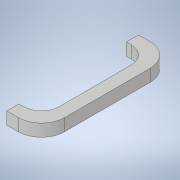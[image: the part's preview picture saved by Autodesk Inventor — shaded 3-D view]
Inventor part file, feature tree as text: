
AUTODESK INVENTOR PART (.ipt)
format: ipt  version: 2020 (Build 240168000, 168)  size: 124,416 bytes
history: native  units: mm
features: extrude x1, fillet x1, hole x1, mirror x1, sketch x1
ambient origin geometry x8: Origin, YZ Plane, XZ Plane, XY Plane, X Axis, Y Axis, Z Axis, Center Point
bodies: Solid1 (feature_tree)
feature tree (5):
  extrude  "Extrusion1"  Depth=30.0mm
  fillet  "Fillet2"  Radius=15.0mm
  hole  "Hole2"  [1 undecoded]
  mirror  "Mirror2"
  sketch  "Sketch1"  dims[d0=114.0mm d1=30.0mm d4=15.0mm d5=10.606602mm d6=10.606602mm d7=0.0mm d17=92.786797mm d18=103.262661mm d19=20.0mm d20=15.0mm d21=4.2mm d22=6.0mm d23=4.0mm d24=2.0mm d25=90.0deg d26=8.0mm d27=20.594885mm]
note: 1 required parameter value undecoded (feature->parameter linkage not recoverable at this tier; creation-order binding heuristic only, values carry confidence <= 0.55)
